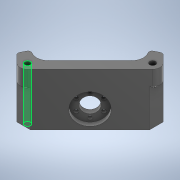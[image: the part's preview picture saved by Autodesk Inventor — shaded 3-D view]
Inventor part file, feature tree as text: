
AUTODESK INVENTOR PART (.ipt)
format: ipt  version: 2020 (Build 240168000, 168)  size: 612,864 bytes
history: native  units: mm
features: sketch x9, extrude x8, chamfer x3, projected_geometry x3, other x1, fillet x1
ambient origin geometry x8: Origin, YZ Plane, XZ Plane, XY Plane, X Axis, Y Axis, Z Axis, Center Point
bodies: Body1 (feature_tree)
feature tree (25):
  other  "Твердое тело1"
  extrude  "Выдавливание1"  Depth=35.0mm TaperAngle=0.0deg
  sketch  "Эскиз2"
  extrude  "Выдавливание4"  Depth=20.6mm
  extrude  "Выдавливание5"  Depth=15.0mm
  sketch  "Эскиз5"
  extrude  "Выдавливание8"  Depth=2.5mm
  extrude  "Выдавливание9"  Depth=60.0mm TaperAngle=360.0deg
  chamfer  "Фаска2"  Distance=11.0mm
  sketch  "Эскиз6"
  extrude  "Выдавливание10"  Depth=4.0mm
  fillet  "Сопряжение1"  Radius=4.0mm
  extrude  "Выдавливание11"  Depth=40.5mm TaperAngle=0.0deg
  extrude  "Выдавливание12"  Depth=4.0mm
  chamfer  "Фаска3"  Distance=4.0mm
  chamfer  "Фаска4"  Distance=3.5mm
  sketch  "Эскиз1"
  projected_geometry  "Спроецированная петля1"
  sketch  "Эскиз3"
  sketch  "Эскиз4"
  projected_geometry  "Спроецированная петля2"
  sketch  "Эскиз7"
  sketch  "Эскиз8"
  projected_geometry  "Спроецированная петля3"
  sketch  "Эскиз9"
